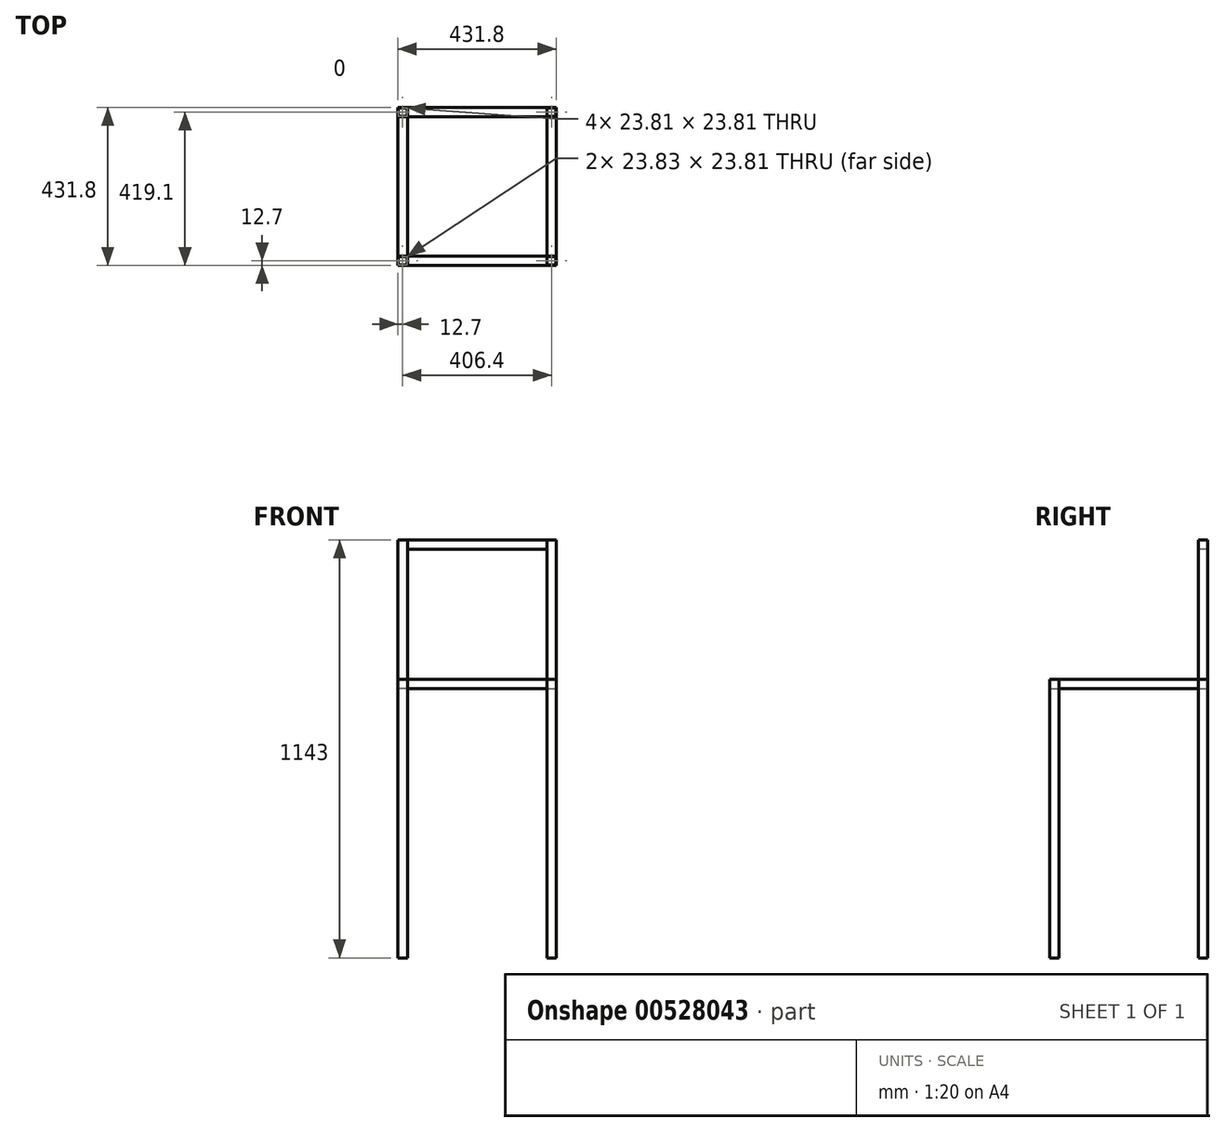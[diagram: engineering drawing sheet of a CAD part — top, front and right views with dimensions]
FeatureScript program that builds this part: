
annotation { "Feature Type Name" : "Feature", "Feature Type Description" : "" }
export const myFeature = defineFeature(function(context is Context, id is Id, definition is map)
    precondition{}
    {
        {
            var Q0;
            Q0=qCreatedBy(makeId("Top.planeOp"),FACE);
            var sketch = newSketch(context, id + "F0", { "sketchPlane" : qUnion([Q0])});
            skLineSegment(sketch, "E0.bottom", {"start": v(-190.5, -12.7) * mm, "end": v(-215.9, -12.7) * mm});
            skLineSegment(sketch, "E0.top", {"start": v(-190.5, 12.7) * mm, "end": v(-215.9, 12.7) * mm});
            skLineSegment(sketch, "E0.left", {"start": v(-190.5, -12.7) * mm, "end": v(-190.5, 12.7) * mm});
            skLineSegment(sketch, "E0.right", {"start": v(-215.9, -12.7) * mm, "end": v(-215.9, 12.7) * mm});
            skPoint(sketch, "E0.middle", {"position": v(-203.2, 0) * mm});
            skLineSegment(sketch, "E1.bottom", {"start": v(-191.3, -11.9) * mm, "end": v(-215.1, -11.9) * mm});
            skLineSegment(sketch, "E1.top", {"start": v(-191.3, 11.9) * mm, "end": v(-215.1, 11.9) * mm});
            skLineSegment(sketch, "E1.left", {"start": v(-191.3, -11.9) * mm, "end": v(-191.3, 11.9) * mm});
            skLineSegment(sketch, "E1.right", {"start": v(-215.1, -11.9) * mm, "end": v(-215.1, 11.9) * mm});
            skLineSegment(sketch, "E2.MirrorCS", {"start": v(190.5, -12.7) * mm, "end": v(190.5, 12.7) * mm});
            skLineSegment(sketch, "E3.MirrorCS", {"start": v(191.3, -11.9) * mm, "end": v(191.3, 11.9) * mm});
            skLineSegment(sketch, "E4.MirrorCS", {"start": v(191.3, 11.9) * mm, "end": v(215.1, 11.9) * mm});
            skLineSegment(sketch, "E5.MirrorCS", {"start": v(190.5, 12.7) * mm, "end": v(215.9, 12.7) * mm});
            skLineSegment(sketch, "E6.MirrorCS", {"start": v(191.3, -11.9) * mm, "end": v(215.1, -11.9) * mm});
            skLineSegment(sketch, "E7.MirrorCS", {"start": v(190.5, -12.7) * mm, "end": v(215.9, -12.7) * mm});
            skLineSegment(sketch, "E8.MirrorCS", {"start": v(215.9, -12.7) * mm, "end": v(215.9, 12.7) * mm});
            skLineSegment(sketch, "E9.MirrorCS", {"start": v(215.1, -11.9) * mm, "end": v(215.1, 11.9) * mm});
            skLineSegment(sketch, "E10.bottom", {"start": v(-190.5, -419.1) * mm, "end": v(-215.9, -419.1) * mm});
            skLineSegment(sketch, "E10.top", {"start": v(-190.5, -393.7) * mm, "end": v(-215.9, -393.7) * mm});
            skLineSegment(sketch, "E10.left", {"start": v(-190.5, -419.1) * mm, "end": v(-190.5, -393.7) * mm});
            skLineSegment(sketch, "E10.right", {"start": v(-215.9, -419.1) * mm, "end": v(-215.9, -393.7) * mm});
            skPoint(sketch, "E10.middle", {"position": v(-203.2, -406.4) * mm});
            skLineSegment(sketch, "E11.bottom", {"start": v(-191.29, -418.3) * mm, "end": v(-215.11, -418.3) * mm});
            skLineSegment(sketch, "E11.top", {"start": v(-191.29, -394.5) * mm, "end": v(-215.11, -394.5) * mm});
            skLineSegment(sketch, "E11.left", {"start": v(-191.29, -418.3) * mm, "end": v(-191.29, -394.5) * mm});
            skLineSegment(sketch, "E11.right", {"start": v(-215.11, -418.3) * mm, "end": v(-215.11, -394.5) * mm});
            skLineSegment(sketch, "E12.MirrorCS", {"start": v(190.5, -419.1) * mm, "end": v(190.5, -393.7) * mm});
            skLineSegment(sketch, "E13.MirrorCS", {"start": v(191.29, -418.3) * mm, "end": v(191.29, -394.5) * mm});
            skLineSegment(sketch, "E14.MirrorCS", {"start": v(191.29, -394.5) * mm, "end": v(215.11, -394.5) * mm});
            skLineSegment(sketch, "E15.MirrorCS", {"start": v(190.5, -393.7) * mm, "end": v(215.9, -393.7) * mm});
            skLineSegment(sketch, "E16.MirrorCS", {"start": v(215.11, -418.3) * mm, "end": v(215.11, -394.5) * mm});
            skLineSegment(sketch, "E17.MirrorCS", {"start": v(215.9, -419.1) * mm, "end": v(215.9, -393.7) * mm});
            skLineSegment(sketch, "E18.MirrorCS", {"start": v(191.29, -418.3) * mm, "end": v(215.11, -418.3) * mm});
            skLineSegment(sketch, "E19.MirrorCS", {"start": v(190.5, -419.1) * mm, "end": v(215.9, -419.1) * mm});
            skSolve(sketch);
        }
        {
            var Q0;
            Q0 = qSketchRegion(id + "F0", true);
            extrude(context, id + "F1", {"entities" : qUnion([Q0]), "depth" : 1143 * mm, "offsetDistance" : 25.4 * mm});
        }
        {
            var Q0;
            Q0=makeQuery(id+"F1.opExtrude","SWEPT_FACE",FACE,{"disambiguationData":[OSD([sQuery(id+"F0.wireOp",EDGE,"E0.bottom")])]});
            var sketch = newSketch(context, id + "F2", { "sketchPlane" : qUnion([Q0])});
            skLineSegment(sketch, "E20.bottom", {"start": v(-190.5, 762) * mm, "end": v(-215.9, 762) * mm});
            skLineSegment(sketch, "E20.top", {"start": v(-190.5, 736.6) * mm, "end": v(-215.9, 736.6) * mm});
            skLineSegment(sketch, "E20.left", {"start": v(-190.5, 762) * mm, "end": v(-190.5, 736.6) * mm});
            skLineSegment(sketch, "E20.right", {"start": v(-215.9, 762) * mm, "end": v(-215.9, 736.6) * mm});
            skPoint(sketch, "E20.middle", {"position": v(-203.2, 749.3) * mm});
            skSolve(sketch);
        }
        {
            var Q0;
            Q0=makeQuery(id+"F2.imprint","IMPRINT",FACE,{"disambiguationData":[TD([[makeQuery(id+"F2.imprint","IMPRINT",EDGE,{"derivedFrom":sQuery(id+"F2.wireOp",EDGE,"E20.bottom")}),1.0]])]});
            extrude(context, id + "F3", {"entities" : qUnion([Q0]), "depth" : 381 * mm, "offsetDistance" : 25.4 * mm});
        }
        {
            var Q0;
            Q0=makeQuery(id+"F3.opExtrude","SWEPT_BODY",BODY,{"disambiguationData":[OSD([sQuery(id+"F2.wireOp",EDGE,"E20.bottom"),sQuery(id+"F2.wireOp",EDGE,"E20.top"),sQuery(id+"F2.wireOp",EDGE,"E20.left"),sQuery(id+"F2.wireOp",EDGE,"E20.right")])]});
            var Q1;
            Q1=qCreatedBy(makeId("Right.planeOp"),FACE);
            mirror(context, id + "F4", {"entities" : qUnion([Q0]), "mirrorPlane" : qUnion([Q1])});
        }
        {
            var Q0;
            Q0=makeQuery(id+"F1.opExtrude","SWEPT_BODY",BODY,{"disambiguationData":[OSD([sQuery(id+"F0.wireOp",EDGE,"E12.MirrorCS"),sQuery(id+"F0.wireOp",EDGE,"E13.MirrorCS"),sQuery(id+"F0.wireOp",EDGE,"E14.MirrorCS"),sQuery(id+"F0.wireOp",EDGE,"E15.MirrorCS"),sQuery(id+"F0.wireOp",EDGE,"E16.MirrorCS"),sQuery(id+"F0.wireOp",EDGE,"E17.MirrorCS"),sQuery(id+"F0.wireOp",EDGE,"E18.MirrorCS"),sQuery(id+"F0.wireOp",EDGE,"E19.MirrorCS")])]});
            deleteBodies(context, id + "F5", {"entities" : qUnion([Q0])});
        }
        {
            var Q0;
            Q0=makeQuery(id+"F1.opExtrude","SWEPT_BODY",BODY,{"disambiguationData":[OSD([sQuery(id+"F0.wireOp",EDGE,"E10.bottom"),sQuery(id+"F0.wireOp",EDGE,"E10.top"),sQuery(id+"F0.wireOp",EDGE,"E10.left"),sQuery(id+"F0.wireOp",EDGE,"E10.right"),sQuery(id+"F0.wireOp",EDGE,"E11.bottom"),sQuery(id+"F0.wireOp",EDGE,"E11.top"),sQuery(id+"F0.wireOp",EDGE,"E11.left"),sQuery(id+"F0.wireOp",EDGE,"E11.right")])]});
            deleteBodies(context, id + "F6", {"entities" : qUnion([Q0])});
        }
        {
            var Q0;
            Q0 = qSketchRegion(id + "F0", true);
            extrude(context, id + "F7", {"entities" : qUnion([Q0]), "depth" : 762 * mm, "offsetDistance" : 25.4 * mm});
        }
        {
            var Q0;
            Q0=makeQuery(id+"F7.opExtrude","SWEPT_FACE",FACE,{"disambiguationData":[OSD([sQuery(id+"F0.wireOp",EDGE,"E10.left")])]});
            var sketch = newSketch(context, id + "F8", { "sketchPlane" : qUnion([Q0])});
            skLineSegment(sketch, "E21.bottom", {"start": v(-419.1, 736.6) * mm, "end": v(-393.7, 736.6) * mm});
            skLineSegment(sketch, "E21.top", {"start": v(-419.1, 762) * mm, "end": v(-393.7, 762) * mm});
            skLineSegment(sketch, "E21.left", {"start": v(-419.1, 736.6) * mm, "end": v(-419.1, 762) * mm});
            skLineSegment(sketch, "E21.right", {"start": v(-393.7, 736.6) * mm, "end": v(-393.7, 762) * mm});
            skPoint(sketch, "E21.middle", {"position": v(-406.4, 749.3) * mm});
            skSolve(sketch);
        }
        {
            var Q0;
            Q0=makeQuery(id+"F8.imprint","IMPRINT",FACE,{"disambiguationData":[TD([[makeQuery(id+"F8.imprint","IMPRINT",EDGE,{"derivedFrom":sQuery(id+"F8.wireOp",EDGE,"E21.bottom")}),1.0]])]});
            extrude(context, id + "F9", {"entities" : qUnion([Q0]), "depth" : 381 * mm, "offsetDistance" : 25.4 * mm});
        }
        {
            var Q0;
            Q0=makeQuery(id+"F1.opExtrude","SWEPT_FACE",FACE,{"disambiguationData":[OSD([sQuery(id+"F0.wireOp",EDGE,"E0.left")])]});
            var sketch = newSketch(context, id + "F10", { "sketchPlane" : qUnion([Q0])});
            skLineSegment(sketch, "E22.bottom", {"start": v(-12.7, 1027.99) * mm, "end": v(12.7, 1027.99) * mm});
            skLineSegment(sketch, "E22.top", {"start": v(-12.7, 1066.2) * mm, "end": v(12.7, 1066.2) * mm});
            skLineSegment(sketch, "E22.left", {"start": v(-12.7, 1027.99) * mm, "end": v(-12.7, 1066.2) * mm});
            skLineSegment(sketch, "E22.right", {"start": v(12.7, 1027.99) * mm, "end": v(12.7, 1066.2) * mm});
            skPoint(sketch, "E22.middle", {"position": v(0, 1047.1) * mm});
            skLineSegment(sketch, "E23.bottom", {"start": v(-12.7, 762) * mm, "end": v(12.7, 762) * mm});
            skLineSegment(sketch, "E23.top", {"start": v(-12.7, 736.6) * mm, "end": v(12.7, 736.6) * mm});
            skLineSegment(sketch, "E23.left", {"start": v(-12.7, 762) * mm, "end": v(-12.7, 736.6) * mm});
            skLineSegment(sketch, "E23.right", {"start": v(12.7, 762) * mm, "end": v(12.7, 736.6) * mm});
            skPoint(sketch, "E23.middle", {"position": v(0, 749.3) * mm});
            skSolve(sketch);
        }
        {
            var Q0;
            Q0 = qSketchRegion(id + "F10", true);
            extrude(context, id + "F11", {"entities" : qUnion([Q0]), "depth" : 381 * mm, "offsetDistance" : 25.4 * mm});
        }
        {
            var Q0;
            Q0=makeQuery(id+"F11.opExtrude","SWEPT_BODY",BODY,{"disambiguationData":[OSD([sQuery(id+"F10.wireOp",EDGE,"E22.bottom"),sQuery(id+"F10.wireOp",EDGE,"E22.top"),sQuery(id+"F10.wireOp",EDGE,"E22.left"),sQuery(id+"F10.wireOp",EDGE,"E22.right")])]});
            deleteBodies(context, id + "F12", {"entities" : qUnion([Q0])});
        }
        {
            var Q0;
            Q0=makeQuery(id+"F1.opExtrude","SWEPT_FACE",FACE,{"disambiguationData":[OSD([sQuery(id+"F0.wireOp",EDGE,"E0.left")])]});
            var sketch = newSketch(context, id + "F13", { "sketchPlane" : qUnion([Q0])});
            skLineSegment(sketch, "E24.bottom", {"start": v(12.7, 1143) * mm, "end": v(-12.7, 1143) * mm});
            skLineSegment(sketch, "E24.top", {"start": v(12.7, 1117.6) * mm, "end": v(-12.7, 1117.6) * mm});
            skLineSegment(sketch, "E24.left", {"start": v(12.7, 1143) * mm, "end": v(12.7, 1117.6) * mm});
            skLineSegment(sketch, "E24.right", {"start": v(-12.7, 1143) * mm, "end": v(-12.7, 1117.6) * mm});
            skPoint(sketch, "E24.middle", {"position": v(0, 1130.3) * mm});
            skLineSegment(sketch, "E25", {"start": v(-12.7, 1117.6) * mm, "end": v(-11.11, 1117.6) * mm});
            skLineSegment(sketch, "E26", {"start": v(-11.11, 1117.6) * mm, "end": v(-11.11, 762.26) * mm});
            skLineSegment(sketch, "E27", {"start": v(-12.7, 762.26) * mm, "end": v(-12.7, 1117.6) * mm});
            skSolve(sketch);
        }
        {
            var Q0;
            Q0 = qSketchRegion(id + "F13", true);
            extrude(context, id + "F14", {"entities" : qUnion([Q0]), "depth" : 381 * mm, "offsetDistance" : 25.4 * mm});
        }
        {
            var Q0;
            Q0=sQuery(id+"F13.wireOp",EDGE,"E26");
            extrude(context, id + "F15", {"bodyType" : ToolBodyType.SURFACE, "surfaceEntities" : qUnion([Q0]), "depth" : 381 * mm, "offsetDistance" : 25.4 * mm});
        }
    });
